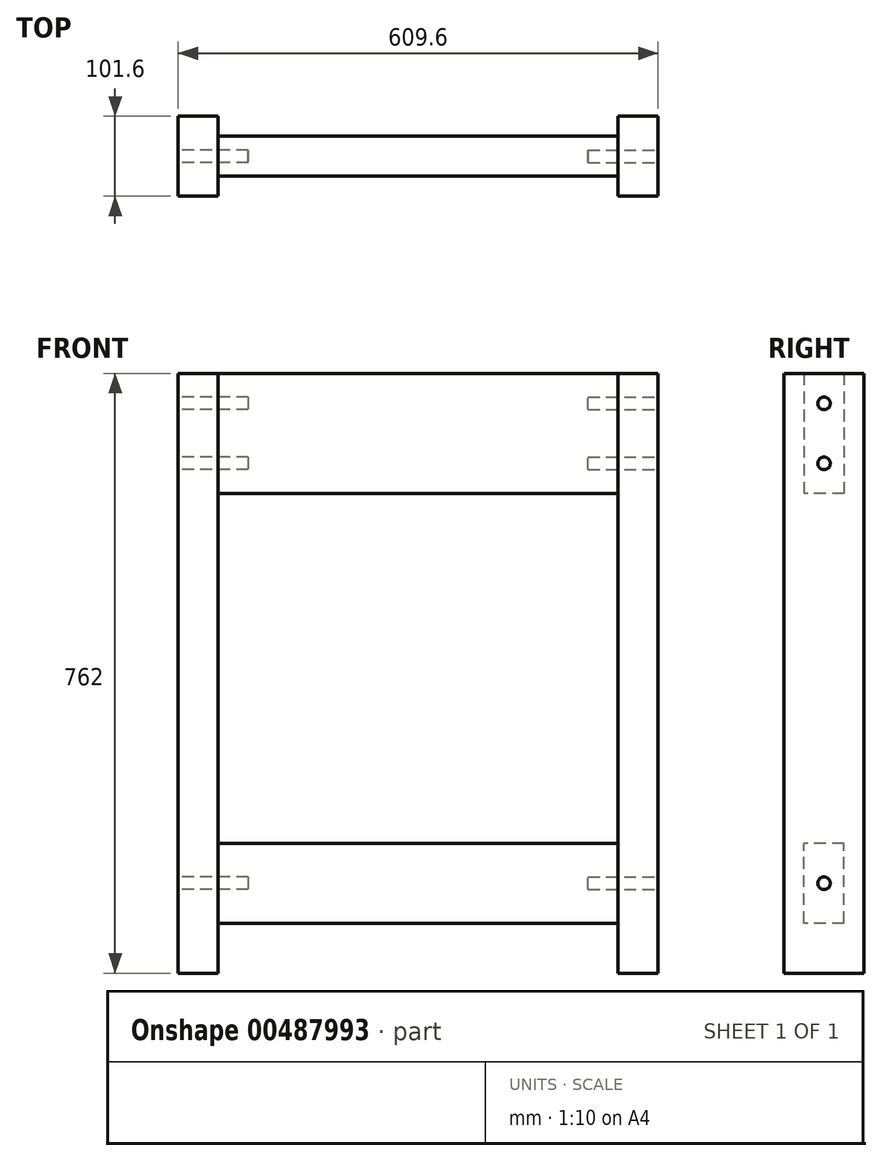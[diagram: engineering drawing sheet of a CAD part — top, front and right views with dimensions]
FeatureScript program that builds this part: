
annotation { "Feature Type Name" : "Feature", "Feature Type Description" : "" }
export const myFeature = defineFeature(function(context is Context, id is Id, definition is map)
    precondition{}
    {
        {
            var Q0;
            Q0=qCreatedBy(makeId("Front.planeOp"),FACE);
            cPlane(context, id + "F0", {"entities" : qUnion([Q0]), "cplaneType" : CPlaneType.OFFSET, "offset" : 25.4 * mm, "width" : 152.4 * mm, "height" : 152.4 * mm});
        }
        {
            var Q0;
            Q0=qCreatedBy(id+"F0.planeOp",FACE);
            var sketch = newSketch(context, id + "F1", { "sketchPlane" : qUnion([Q0])});
            skLineSegment(sketch, "E0.bottom", {"start": v(245.49, 76.2) * mm, "end": v(-262.51, 76.2) * mm});
            skLineSegment(sketch, "E0.top", {"start": v(245.49, -76.2) * mm, "end": v(-262.51, -76.2) * mm});
            skLineSegment(sketch, "E0.left", {"start": v(245.49, 76.2) * mm, "end": v(245.49, -76.2) * mm});
            skLineSegment(sketch, "E0.right", {"start": v(-262.51, 76.2) * mm, "end": v(-262.51, -76.2) * mm});
            skPoint(sketch, "E0.middle", {"position": v(-8.51, 0) * mm});
            skSolve(sketch);
        }
        {
            var Q0;
            Q0 = qSketchRegion(id + "F1", true);
            extrude(context, id + "F2", {"entities" : qUnion([Q0]), "oppositeDirection" : true, "depth" : 50.8 * mm});
        }
        {
            var Q0;
            Q0=makeQuery(id+"F2.opExtrude","SWEPT_FACE",FACE,{"disambiguationData":[OSD([sQuery(id+"F1.wireOp",EDGE,"E0.left")])]});
            var sketch = newSketch(context, id + "F3", { "sketchPlane" : qUnion([Q0])});
            skLineSegment(sketch, "E1.bottom", {"start": v(50.8, -685.8) * mm, "end": v(-50.8, -685.8) * mm});
            skLineSegment(sketch, "E1.top", {"start": v(50.8, 76.2) * mm, "end": v(-50.8, 76.2) * mm});
            skLineSegment(sketch, "E1.left", {"start": v(50.8, -685.8) * mm, "end": v(50.8, 76.2) * mm});
            skLineSegment(sketch, "E1.right", {"start": v(-50.8, -685.8) * mm, "end": v(-50.8, 76.2) * mm});
            skPoint(sketch, "E1.middle", {"position": v(0, -304.8) * mm});
            skPoint(sketch, "E2.0", {"position": v(0, 76.2) * mm});
            skSolve(sketch);
        }
        {
            var Q0;
            Q0 = qSketchRegion(id + "F3", true);
            extrude(context, id + "F4", {"entities" : qUnion([Q0]), "depth" : 50.8 * mm});
        }
        {
            var Q0;
            Q0=makeQuery(id+"F2.opExtrude","SWEPT_FACE",FACE,{"disambiguationData":[OSD([sQuery(id+"F1.wireOp",EDGE,"E0.right")])]});
            var sketch = newSketch(context, id + "F5", { "sketchPlane" : qUnion([Q0])});
            skLineSegment(sketch, "E3.bottom", {"start": v(50.8, -685.8) * mm, "end": v(-50.8, -685.8) * mm});
            skLineSegment(sketch, "E3.top", {"start": v(50.8, 76.2) * mm, "end": v(-50.8, 76.2) * mm});
            skLineSegment(sketch, "E3.left", {"start": v(50.8, -685.8) * mm, "end": v(50.8, 76.2) * mm});
            skLineSegment(sketch, "E3.right", {"start": v(-50.8, -685.8) * mm, "end": v(-50.8, 76.2) * mm});
            skPoint(sketch, "E3.middle", {"position": v(0, -304.8) * mm});
            skPoint(sketch, "E4.0", {"position": v(0, 76.2) * mm});
            skSolve(sketch);
        }
        {
            var Q0;
            Q0 = qSketchRegion(id + "F5", true);
            extrude(context, id + "F6", {"entities" : qUnion([Q0]), "depth" : 50.8 * mm});
        }
        {
            var Q0;
            Q0=qCreatedBy(makeId("Front.planeOp"),FACE);
            cPlane(context, id + "F7", {"entities" : qUnion([Q0]), "cplaneType" : CPlaneType.OFFSET, "offset" : 25.4 * mm, "width" : 152.4 * mm, "height" : 152.4 * mm});
        }
        {
            var Q0;
            Q0=qCreatedBy(id+"F7.planeOp",FACE);
            var sketch = newSketch(context, id + "F8", { "sketchPlane" : qUnion([Q0])});
            skPoint(sketch, "E5.0", {"position": v(-262.51, -685.8) * mm});
            skPoint(sketch, "E6.0", {"position": v(245.49, -685.8) * mm});
            skLineSegment(sketch, "E7", {"start": v(-262.51, -685.8) * mm, "end": v(-262.51, -622.3) * mm, "construction": true});
            skLineSegment(sketch, "E8.bottom", {"start": v(-262.51, -622.3) * mm, "end": v(245.49, -622.3) * mm});
            skLineSegment(sketch, "E8.top", {"start": v(-262.51, -520.7) * mm, "end": v(245.49, -520.7) * mm});
            skLineSegment(sketch, "E8.left", {"start": v(-262.51, -622.3) * mm, "end": v(-262.51, -520.7) * mm});
            skLineSegment(sketch, "E8.right", {"start": v(245.49, -622.3) * mm, "end": v(245.49, -520.7) * mm});
            skSolve(sketch);
        }
        {
            var Q0;
            Q0 = qSketchRegion(id + "F8", true);
            extrude(context, id + "F9", {"entities" : qUnion([Q0]), "oppositeDirection" : true, "depth" : 50.8 * mm});
        }
        {
            var Q0;
            Q0=makeQuery(id+"F4.opExtrude","CAP_FACE",FACE,{"disambiguationData":[OSD([sQuery(id+"F3.wireOp",EDGE,"E1.bottom"),sQuery(id+"F3.wireOp",EDGE,"E1.top"),sQuery(id+"F3.wireOp",EDGE,"E1.left"),sQuery(id+"F3.wireOp",EDGE,"E1.right")])],"isStart":false});
            var sketch = newSketch(context, id + "F10", { "sketchPlane" : qUnion([Q0])});
            skPoint(sketch, "E9.0", {"position": v(-25.4, -76.2) * mm});
            skPoint(sketch, "E10.0", {"position": v(25.4, -76.2) * mm});
            skPoint(sketch, "E11.0", {"position": v(25.4, 76.2) * mm});
            skPoint(sketch, "E12.0", {"position": v(-25.4, 76.2) * mm});
            skPoint(sketch, "E13.0", {"position": v(0, 76.2) * mm});
            skPoint(sketch, "E14.0", {"position": v(0, -76.2) * mm});
            skPoint(sketch, "E15.0", {"position": v(0, 0) * mm});
            skLineSegment(sketch, "E16", {"start": v(0, 0) * mm, "end": v(0, 76.2) * mm, "construction": true});
            skLineSegment(sketch, "E17", {"start": v(0, 0) * mm, "end": v(0, -76.2) * mm, "construction": true});
            skCircle(sketch, "E18", {"center": v(0, 38.1) * mm, "radius": 7.94 * mm});
            skLineSegment(sketch, "E19", {"start": v(-23.77, 0) * mm, "end": v(25.61, 0) * mm, "construction": true});
            skCircle(sketch, "E20.MirrorC", {"center": v(0, -38.1) * mm, "radius": 7.94 * mm});
            skPoint(sketch, "E21.0", {"position": v(0, -520.7) * mm});
            skPoint(sketch, "E22.0", {"position": v(25.4, -571.5) * mm});
            skPoint(sketch, "E23.0", {"position": v(-25.4, -571.5) * mm});
            skPoint(sketch, "E24.0", {"position": v(0, -622.3) * mm});
            skCircle(sketch, "E25", {"center": v(0, -571.5) * mm, "radius": 7.94 * mm});
            skLineSegment(sketch, "E26", {"start": v(0, -520.7) * mm, "end": v(0, -622.3) * mm, "construction": true});
            skSolve(sketch);
        }
        {
            var Q0;
            Q0 = qSketchRegion(id + "F10", true);
            extrude(context, id + "F11", {"entities" : qUnion([Q0]), "oppositeDirection" : true, "depth" : 88.9 * mm});
        }
        {
            var Q0;
            Q0=makeQuery(id+"F6.opExtrude","CAP_FACE",FACE,{"disambiguationData":[OSD([sQuery(id+"F5.wireOp",EDGE,"E3.bottom"),sQuery(id+"F5.wireOp",EDGE,"E3.top"),sQuery(id+"F5.wireOp",EDGE,"E3.left"),sQuery(id+"F5.wireOp",EDGE,"E3.right")])],"isStart":false});
            var sketch = newSketch(context, id + "F12", { "sketchPlane" : qUnion([Q0])});
            skPoint(sketch, "E27.0", {"position": v(0, 76.2) * mm});
            skPoint(sketch, "E28.0", {"position": v(0, -76.2) * mm});
            skPoint(sketch, "E29.0", {"position": v(0, 0) * mm});
            skLineSegment(sketch, "E30", {"start": v(0, -76.2) * mm, "end": v(0, 0) * mm, "construction": true});
            skLineSegment(sketch, "E31", {"start": v(0, 0) * mm, "end": v(0, 76.2) * mm, "construction": true});
            skPoint(sketch, "E32.0", {"position": v(-25.4, 0) * mm});
            skPoint(sketch, "E33.0", {"position": v(25.4, 0) * mm});
            skLineSegment(sketch, "E34", {"start": v(-25.4, 0) * mm, "end": v(25.4, 0) * mm, "construction": true});
            skCircle(sketch, "E35", {"center": v(0, 38.1) * mm, "radius": 7.94 * mm});
            skCircle(sketch, "E36.MirrorC", {"center": v(0, -38.1) * mm, "radius": 7.94 * mm});
            skPoint(sketch, "E37.0", {"position": v(0, -520.7) * mm});
            skPoint(sketch, "E38.0", {"position": v(0, -622.3) * mm});
            skLineSegment(sketch, "E39", {"start": v(0, -622.3) * mm, "end": v(0, -520.7) * mm, "construction": true});
            skCircle(sketch, "E40", {"center": v(0, -571.5) * mm, "radius": 7.94 * mm});
            skSolve(sketch);
        }
        {
            var Q0;
            Q0 = qSketchRegion(id + "F12", true);
            extrude(context, id + "F13", {"entities" : qUnion([Q0]), "oppositeDirection" : true, "depth" : 88.9 * mm});
        }
    });
